# Revit family: Domotics-DomesticRanges-GEWISS-SYSTEM_DATA-SOCKET-OUTLET_RJ45_COVER
name_source: partatom
category: Apparecchi elettrici
revit_build: Autodesk Revit 2016 (Build: 20161004_0715(x64)
units: mm (PartAtom-declared; Revit-internal decimal feet)

## family parameters
Condiviso = Sì
Host = Superficie
Mantenere orientamento annotazione = Sì
Numero OmniClass = 23.80.50.14
Punto di calcolo locali = Sì
Quota connettore circolare = Usa diametro
Taglio con vuoti quando caricato = Sì
Tipo di parte = Normale
Titolo OmniClass = Plug Connectors

## types (6) — shared parameters
Carico apparente = 0 VA
Catalogue = DOMOTICS
Catalogue Range = SYSTEM - DOMESTIC RANGE
Electrocod = 3722
IDF = ce7dd9a2-14bb-4f00-bfab-9609d56ead63
IDT = febde81f-cc29-43ff-b45b-0408f406c939
Immagine tipo = GW21270.jpg
Larghezza presa = 23 mm  [stored 0.0754593 ft]
N. poli = 1
No. SYSTEM modules = 1
Produttore = GEWISS S.p.A.
Prospetto di default = 1219 mm
SEO = Enclosure
Simbolo = SIMBOLO PRESE TELEFONO : PRESA TEL
Technical sheet = https://www.gewiss.com
Tipo_ = SYSTEM PRESE RJ45_BASE : GW21270 Contenitore vuoto RJ45 Cat.5 UTP AMP nero
URL = https://www.gewiss.com
Version file RFA = 19.4
Volt = 230 V

## per-type parameters (varying)
| type | Colour | Compatibility | Description. | Descrizione | EAN code | Modello |
| GW21266 - ENCLOSURE FOR RJ45 IBM SY/BK | Black | IBM | IBM unwired container | ENCLOSURE FOR RJ45 IBM SY/BK | 8011564128958 | GW21266 |
| GW20266 - ENCLOSURE FOR RJ45 IBM SY/WT | White | IBM | IBM unwired container | ENCLOSURE FOR RJ45 IBM SY/WT | 8011564045835 | GW20266 |
| GW21267 - ENCLOSURE FOR RJ45 AVAYA SY/BK | Black | SYSTIMAX COMMSCOPE | AVAYA unwired container | ENCLOSURE FOR RJ45 AVAYA SY/BK | 8011564128972 | GW21267 |
| GW20270 - ENCLOSURE FOR RJ45 AMP SY/WT | White | AMP / Keystone Jack | AMP unwired container | ENCLOSURE FOR RJ45 AMP SY/WT | 8011564071872 | GW20270 |
| GW20267 - ENCLOSURE FOR RJ45 AVAYA SY/WT | White | SYSTIMAX COMMSCOPE | AVAYA unwired container | ENCLOSURE FOR RJ45 AVAYA SY/WT | 8011564045842 | GW20267 |
| GW21270 - ENCLOSURE FOR RJ45 AMP SY/BK | Black | AMP / Keystone Jack | AMP unwired container | ENCLOSURE FOR RJ45 AMP SY/BK | 8011564128989 | GW21270 |

note: [stored X ft] marks values corroborated as IEEE doubles in the binary element streams (Revit-internal decimal feet)

## geometry (parser evidence)
native form markers: Sweep x2
no freeform markers — native parametric forms only
